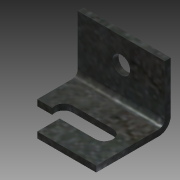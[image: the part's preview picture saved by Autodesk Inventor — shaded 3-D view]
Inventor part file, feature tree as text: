
AUTODESK INVENTOR PART (.ipt)
format: ipt  version: 2015 (Build 190159000, 159)  size: 196,608 bytes
history: native  units: in
note: dims shown in document units (in); Inventor stores cm internally (conversion verified against a paired STEP export)
features: sketch x8, sheet_metal_op x4, other x4, projected_geometry x4, hole x1
ambient origin geometry x8: Origin, YZ Plane, XZ Plane, XY Plane, X Axis, Y Axis, Z Axis, Center Point
bodies: Solid1 (feature_tree)
feature tree (21):
  sheet_metal_op  "Face1"
  sheet_metal_op  "Flange1"
  sketch  "Sketch3"  dims[d3=0.06in]
  hole  "Hole1"  [1 undecoded]
  sketch  "Sketch7"  dims[d5=0.12in]
  sketch  "Sketch8"  dims[d6=0.06in]
  sketch  "Sketch9"  dims[d7=0.625in d8=90.0deg d9=0.06in]
  sketch  "Sketch1"  dims[d0=0.875in d1=0.75in]
  other  "Plate1"
  sketch  "Sketch2"  dims[d2=0.06in]
  other  "Plate2"
  sheet_metal_op  "Bend1"
  sheet_metal_op  "Corner1"
  projected_geometry  "Projected Loop1"
  sketch  "Sketch4"  dims[d4=0.03in]
  projected_geometry  "Projected Loop2"
  projected_geometry  "Projected Loop3"
  projected_geometry  "Projected Loop4"
  sketch  "Sketch10"  dims[d10=0.24in d11=0.06in d12=0.06in d13=0.63in d14=0.875in d15=0.875in d16=0.505in d17=0.177in d18=0.75in d19=0.332in d20=0.25in d21=0.5635in d22=0.06in d23=0.8108in d24=0.177in d25=0.146in d26=0.06in d27=0.0in d28=0.625in d29=0.505in d30=0.875in d31=0.75in d32=0.63in d34=0.203in d35=0.281in d36=0.281in d39=0.281in d40=0.06in d41=0.0in]
  other  "Cut1"
  other  "Cut3"
note: 1 required parameter value undecoded (feature->parameter linkage not recoverable at this tier; creation-order binding heuristic only, values carry confidence <= 0.55)
